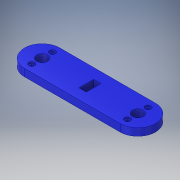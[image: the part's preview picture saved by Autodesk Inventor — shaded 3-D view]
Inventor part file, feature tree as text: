
AUTODESK INVENTOR PART (.ipt)
format: ipt  version: 2017 (Build 210142000, 142)  size: 148,992 bytes
history: native  units: in
note: dims shown in document units (in); Inventor stores cm internally (conversion verified against a paired STEP export)
features: extrude x2, sketch x2
ambient origin geometry x8: Origin, YZ Plane, XZ Plane, XY Plane, X Axis, Y Axis, Z Axis, Center Point
bodies: Body1 (feature_tree)
feature tree (4):
  extrude  "Extrusion7"  Depth=0.9449in
  extrude  "Extrusion8"  Depth=0.0787in
  sketch  "Sketch1"  dims[d5=2.5591in d6=0.9449in]
  sketch  "Sketch4"  dims[d7=0.2953in d17=0.0787in d18=0.2756in d19=0.2756in d25=0.1969in d26=0.3937in d27=0.1969in d28=0.0in d29=0.1575in d30=0.0394in d31=0.0in]
